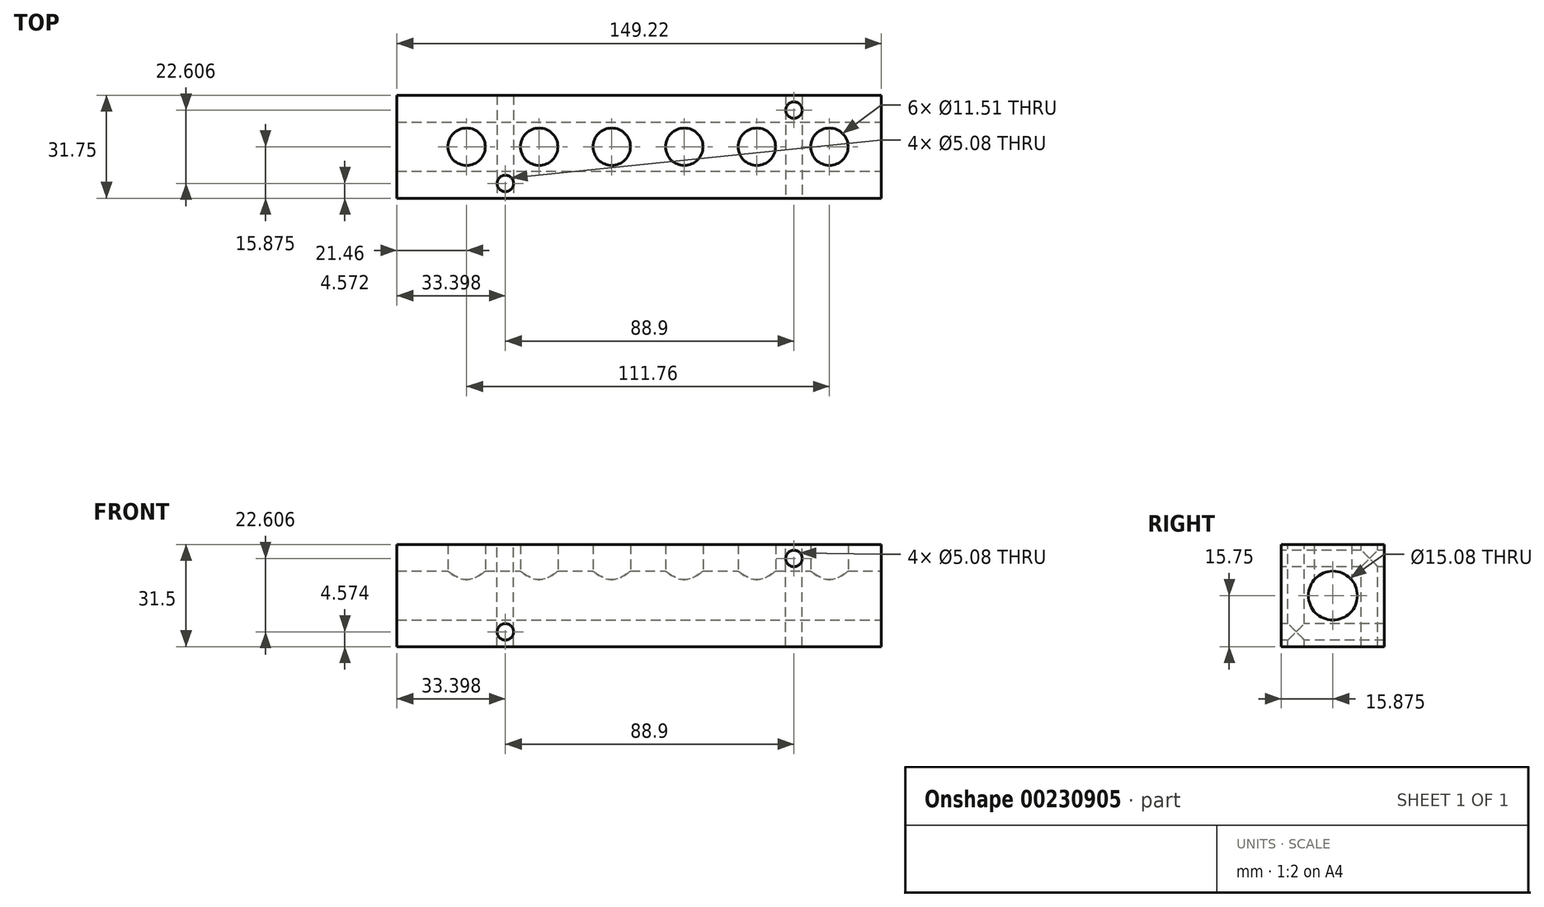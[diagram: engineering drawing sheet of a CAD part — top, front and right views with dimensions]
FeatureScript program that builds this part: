
annotation { "Feature Type Name" : "Feature", "Feature Type Description" : "" }
export const myFeature = defineFeature(function(context is Context, id is Id, definition is map)
    precondition{}
    {
        {
            var Q0;
            Q0=qCreatedBy(makeId("Front.planeOp"),FACE);
            var sketch = newSketch(context, id + "F0", { "sketchPlane" : qUnion([Q0])});
            skLineSegment(sketch, "E0.bottom", {"start": v(74.61, -15.75) * mm, "end": v(-74.61, -15.75) * mm});
            skLineSegment(sketch, "E0.top", {"start": v(74.61, 15.75) * mm, "end": v(-74.61, 15.75) * mm});
            skLineSegment(sketch, "E0.left", {"start": v(74.61, -15.75) * mm, "end": v(74.61, 15.75) * mm});
            skLineSegment(sketch, "E0.right", {"start": v(-74.61, -15.75) * mm, "end": v(-74.61, 15.75) * mm});
            skPoint(sketch, "E0.middle", {"position": v(0, 0) * mm});
            skSolve(sketch);
        }
        {
            var Q0;
            Q0 = qSketchRegion(id + "F0", true);
            extrude(context, id + "F1", {"entities" : qUnion([Q0]), "oppositeDirection" : true, "depth" : 31.75 * mm});
        }
        {
            var Q0;
            Q0=qCreatedBy(makeId("Top.planeOp"),FACE);
            var sketch = newSketch(context, id + "F2", { "sketchPlane" : qUnion([Q0])});
            skLineSegment(sketch, "E1", {"start": v(-74.61, 15.88) * mm, "end": v(74.61, 15.88) * mm, "construction": true});
            skPoint(sketch, "E2", {"position": v(-53.15, 15.88) * mm});
            skPoint(sketch, "E3", {"position": v(-30.8, 15.88) * mm});
            skPoint(sketch, "E4", {"position": v(-8.45, 15.88) * mm});
            skPoint(sketch, "E5", {"position": v(13.9, 15.88) * mm});
            skPoint(sketch, "E6", {"position": v(36.26, 15.88) * mm});
            skPoint(sketch, "E7", {"position": v(58.61, 15.88) * mm});
            skCircle(sketch, "E8", {"center": v(-53.15, 15.88) * mm, "radius": 5.75 * mm});
            skCircle(sketch, "E9", {"center": v(-30.8, 15.88) * mm, "radius": 5.75 * mm});
            skCircle(sketch, "E10", {"center": v(-8.45, 15.88) * mm, "radius": 5.75 * mm});
            skCircle(sketch, "E11", {"center": v(13.9, 15.88) * mm, "radius": 5.75 * mm});
            skCircle(sketch, "E12", {"center": v(36.26, 15.88) * mm, "radius": 5.75 * mm});
            skCircle(sketch, "E13", {"center": v(58.61, 15.88) * mm, "radius": 5.75 * mm});
            skSolve(sketch);
        }
        {
            var Q0;
            Q0 = qSketchRegion(id + "F2", true);
            extrude(context, id + "F3", {"entities" : qUnion([Q0]), "operationType" : NewBodyOperationType.REMOVE, "depth" : 15.88 * mm});
        }
        {
            var Q0;
            Q0=makeQuery(id+"F1.opExtrude","SWEPT_FACE",FACE,{"disambiguationData":[OSD([sQuery(id+"F0.wireOp",EDGE,"E0.left")])]});
            var sketch = newSketch(context, id + "F4", { "sketchPlane" : qUnion([Q0])});
            skLineSegment(sketch, "E14", {"start": v(0, 15.75) * mm, "end": v(31.75, -15.75) * mm, "construction": true});
            skCircle(sketch, "E15", {"center": v(15.88, 0) * mm, "radius": 7.54 * mm});
            skSolve(sketch);
        }
        {
            var Q0;
            Q0 = qSketchRegion(id + "F4", true);
            extrude(context, id + "F5", {"entities" : qUnion([Q0]), "operationType" : NewBodyOperationType.REMOVE, "endBound" : BoundingType.THROUGH_ALL, "oppositeDirection" : true, "depth" : 25.4 * mm});
        }
        {
            var Q0;
            Q0=makeQuery(id+"F1.opExtrude","CAP_FACE",FACE,{"disambiguationData":[OSD([sQuery(id+"F0.wireOp",EDGE,"E0.bottom"),sQuery(id+"F0.wireOp",EDGE,"E0.top"),sQuery(id+"F0.wireOp",EDGE,"E0.left"),sQuery(id+"F0.wireOp",EDGE,"E0.right")])],"isStart":true});
            var sketch = newSketch(context, id + "F6", { "sketchPlane" : qUnion([Q0])});
            skCircle(sketch, "E16", {"center": v(-41.21, -11.18) * mm, "radius": 2.54 * mm});
            skCircle(sketch, "E17", {"center": v(47.69, 11.43) * mm, "radius": 2.54 * mm});
            skSolve(sketch);
        }
        {
            var Q0;
            Q0 = qSketchRegion(id + "F6", true);
            extrude(context, id + "F7", {"entities" : qUnion([Q0]), "operationType" : NewBodyOperationType.REMOVE, "endBound" : BoundingType.THROUGH_ALL, "oppositeDirection" : true, "depth" : 25.4 * mm});
        }
        {
            var Q0;
            Q0=makeQuery(id+"F1.opExtrude","SWEPT_FACE",FACE,{"disambiguationData":[OSD([sQuery(id+"F0.wireOp",EDGE,"E0.top")])]});
            var sketch = newSketch(context, id + "F8", { "sketchPlane" : qUnion([Q0])});
            skCircle(sketch, "E18", {"center": v(47.69, 27.18) * mm, "radius": 2.54 * mm});
            skCircle(sketch, "E19", {"center": v(-41.21, 4.57) * mm, "radius": 2.54 * mm});
            skSolve(sketch);
        }
        {
            var Q0;
            Q0 = qSketchRegion(id + "F8", true);
            extrude(context, id + "F9", {"entities" : qUnion([Q0]), "operationType" : NewBodyOperationType.REMOVE, "endBound" : BoundingType.THROUGH_ALL, "oppositeDirection" : true, "depth" : 25.4 * mm});
        }
    });
